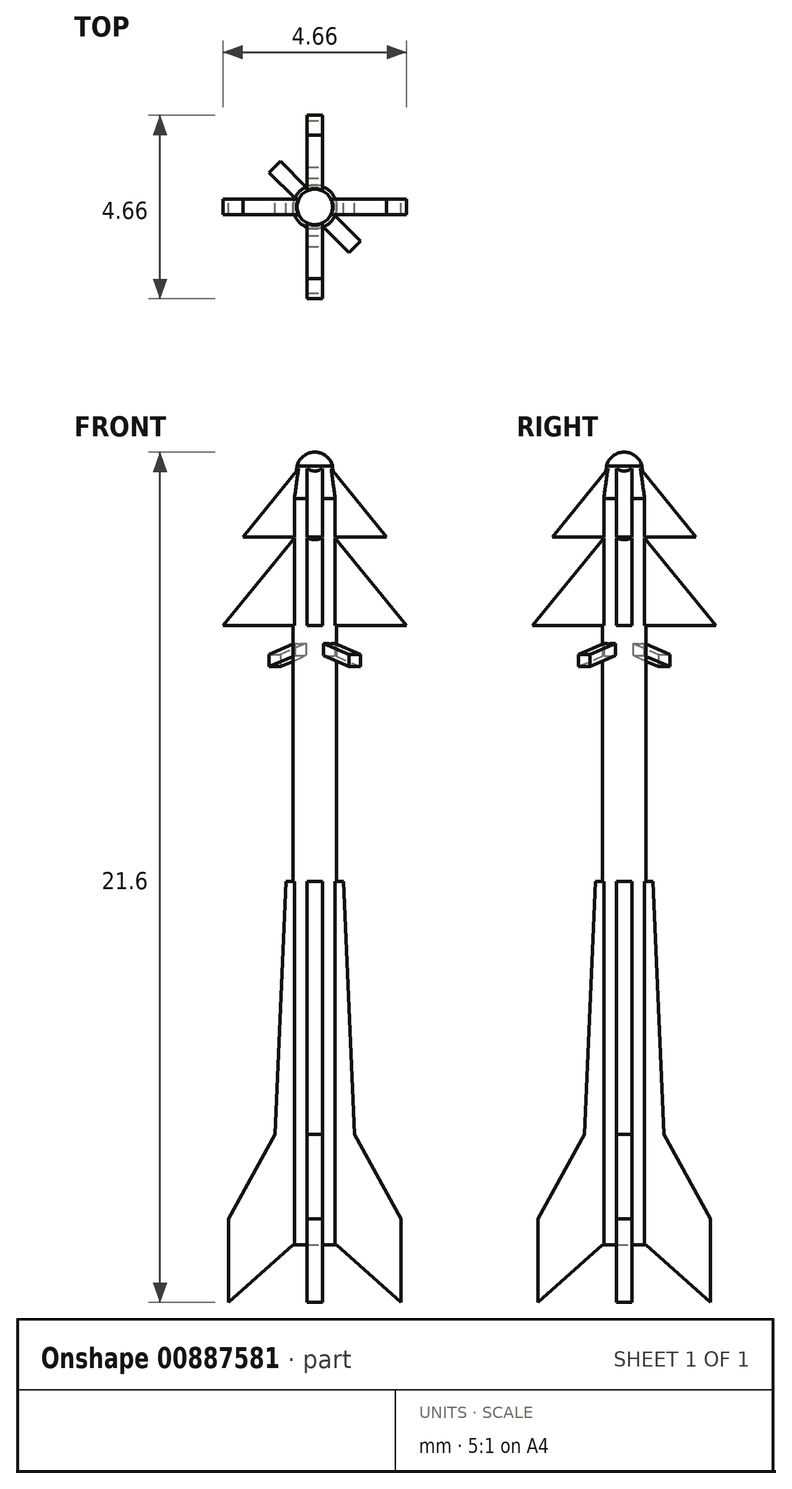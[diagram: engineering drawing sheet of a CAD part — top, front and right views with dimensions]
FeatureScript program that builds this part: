
annotation { "Feature Type Name" : "Feature", "Feature Type Description" : "" }
export const myFeature = defineFeature(function(context is Context, id is Id, definition is map)
    precondition{}
    {
        {
            var Q0;
            Q0=qCreatedBy(makeId("Front.planeOp"),FACE);
            var sketch = newSketch(context, id + "F0", { "sketchPlane" : qUnion([Q0])});
            skLineSegment(sketch, "E0", {"start": v(0, 0) * mm, "end": v(0, 20.14) * mm});
            skLineSegment(sketch, "E1", {"start": v(0.56, 18.96) * mm, "end": v(0.56, 0) * mm});
            skLineSegment(sketch, "E2", {"start": v(0.56, 0) * mm, "end": v(0, 0) * mm});
            skLineSegment(sketch, "E3", {"start": v(0, 20.14) * mm, "end": v(1.85, 20.14) * mm, "construction": true});
            skLineSegment(sketch, "E4", {"start": v(0.56, 18.96) * mm, "end": v(0.45, 19.8) * mm});
            skArc(sketch, "E5", {"start": v(0.45, 19.8) * mm, "mid": v(0.28, 20.04) * mm, "end": v(0, 20.14) * mm});
            skSolve(sketch);
        }
        {
            var Q0;
            Q0=qSketchRegion(id+"F0",true);
            var Q1;
            Q1=sQuery(id+"F0.wireOp",EDGE,"E0");
            revolve(context, id + "F1", {"surfaceOperationType" : NewSurfaceOperationType.NEW, "entities" : qUnion([Q0]), "axis" : qUnion([Q1]), "revolveType" : RevolveType.FULL});
        }
        {
            var Q0;
            Q0=qCreatedBy(makeId("Front.planeOp"),FACE);
            var sketch = newSketch(context, id + "F2", { "sketchPlane" : qUnion([Q0])});
            skLineSegment(sketch, "E6", {"start": v(-0.56, 0.19) * mm, "end": v(-0.56, 18.96) * mm, "construction": true});
            skLineSegment(sketch, "E7.0", {"start": v(0.56, 18.96) * mm, "end": v(-0.56, 18.96) * mm});
            skLineSegment(sketch, "E8", {"start": v(-0.23, 19.96) * mm, "end": v(-1.82, 17.99) * mm});
            skLineSegment(sketch, "E9", {"start": v(-1.82, 17.99) * mm, "end": v(-0.5, 17.99) * mm});
            skLineSegment(sketch, "E10", {"start": v(-0.5, 17.99) * mm, "end": v(-2.33, 15.73) * mm});
            skLineSegment(sketch, "E11", {"start": v(-2.33, 15.73) * mm, "end": v(2.33, 15.73) * mm});
            skLineSegment(sketch, "E12", {"start": v(2.33, 15.73) * mm, "end": v(0.5, 17.99) * mm});
            skLineSegment(sketch, "E13", {"start": v(0.5, 17.99) * mm, "end": v(1.82, 17.99) * mm});
            skLineSegment(sketch, "E14", {"start": v(1.82, 17.99) * mm, "end": v(0.23, 19.96) * mm});
            skLineSegment(sketch, "E15", {"start": v(0.23, 19.96) * mm, "end": v(-0.23, 19.96) * mm});
            skLineSegment(sketch, "E16.0", {"start": v(0.56, 0) * mm, "end": v(-0.56, 0) * mm});
            skLineSegment(sketch, "E17", {"start": v(-0.54, 0.02) * mm, "end": v(-2.19, -1.46) * mm});
            skLineSegment(sketch, "E18", {"start": v(-2.19, -1.46) * mm, "end": v(-2.19, 0.66) * mm});
            skLineSegment(sketch, "E19", {"start": v(-2.19, 0.66) * mm, "end": v(-1, 2.81) * mm});
            skLineSegment(sketch, "E20", {"start": v(-1, 2.81) * mm, "end": v(-0.73, 9.24) * mm});
            skLineSegment(sketch, "E21", {"start": v(-0.73, 9.24) * mm, "end": v(0.73, 9.24) * mm});
            skLineSegment(sketch, "E22", {"start": v(0.73, 9.24) * mm, "end": v(1, 2.81) * mm});
            skLineSegment(sketch, "E23", {"start": v(1, 2.81) * mm, "end": v(2.19, 0.66) * mm});
            skLineSegment(sketch, "E24", {"start": v(2.19, 0.66) * mm, "end": v(2.19, -1.46) * mm});
            skLineSegment(sketch, "E25", {"start": v(2.19, -1.46) * mm, "end": v(0.54, 0.02) * mm});
            skLineSegment(sketch, "E26", {"start": v(0.54, 0.02) * mm, "end": v(-0.54, 0.02) * mm});
            skLineSegment(sketch, "E27", {"start": v(0, 0) * mm, "end": v(0, 0.02) * mm, "construction": true});
            skLineSegment(sketch, "E28", {"start": v(0, 0) * mm, "end": v(0, 9.24) * mm, "construction": true});
            skPoint(sketch, "E28.endSnap0", {"position": v(0, 0) * mm});
            skLineSegment(sketch, "E29", {"start": v(0, 19.96) * mm, "end": v(0, 18.96) * mm, "construction": true});
            skLineSegment(sketch, "E30", {"start": v(0, 18.96) * mm, "end": v(0, 15.73) * mm, "construction": true});
            skPoint(sketch, "E31", {"position": v(-0.56, 17.92) * mm});
            skSolve(sketch);
        }
        {
            var Q0;
            Q0=qSketchRegion(id+"F2",true);
            extrude(context, id + "F3", {"entities" : qUnion([Q0]), "operationType" : NewBodyOperationType.ADD, "depth" : .4 * mm, "offsetDistance" : 25 * mm, "symmetric" : true});
        }
        {
            var Q0;
            Q0=makeQuery(id+"F1.opRevolve","SWEPT_BODY",BODY,{"disambiguationData":[OSD([sQuery(id+"F0.wireOp",EDGE,"E0"),sQuery(id+"F0.wireOp",EDGE,"E1"),sQuery(id+"F0.wireOp",EDGE,"E2"),sQuery(id+"F0.wireOp",EDGE,"m1K1lCZm-MTc8-Btmt-IA6e-LtdyprMEJuD3")])]});
            var Q1;
            Q1=makeQuery(id+"F1.opRevolve","SWEPT_FACE",FACE,{"disambiguationData":[OSD([sQuery(id+"F0.wireOp",EDGE,"E1")])]});
            circularPattern(context, id + "F4", {"entities" : qUnion([Q0]), "axis" : qUnion([Q1]), "angle" : 360 * degree, "instanceCount" : 4, "equalSpace" : true, "computeTransformsWithoutBuiltin" : true});
        }
        {
            var Q0;
            Q0=qCreatedBy(makeId("Front.planeOp"),FACE);
            var Q1;
            Q1=qCreatedBy(makeId("Right.planeOp"),FACE);
            cPlane(context, id + "F5", {"entities" : qUnion([Q0, Q1]), "cplaneType" : CPlaneType.MID_PLANE, "offset" : 25 * mm, "width" : 150 * mm, "height" : 150 * mm});
        }
        {
            var Q0;
            Q0=qCreatedBy(id+"F5.planeOp",FACE);
            var sketch = newSketch(context, id + "F6", { "sketchPlane" : qUnion([Q0])});
            skLineSegment(sketch, "E32", {"start": v(-0.25, 15.37) * mm, "end": v(-1.44, 15) * mm});
            skLineSegment(sketch, "E33", {"start": v(1.44, 15) * mm, "end": v(0.25, 15.37) * mm});
            skLineSegment(sketch, "E34", {"start": v(0.25, 15.37) * mm, "end": v(-0.25, 15.37) * mm});
            skPoint(sketch, "E35", {"position": v(-0.53, 15.28) * mm});
            skLineSegment(sketch, "E36", {"start": v(0, 0) * mm, "end": v(0, 15.05) * mm, "construction": true});
            skPoint(sketch, "E36.endSnap0", {"position": v(0, 15.05) * mm});
            skLineSegment(sketch, "E37", {"start": v(-1.44, 15) * mm, "end": v(-1.44, 14.69) * mm});
            skLineSegment(sketch, "E38", {"start": v(-1.44, 14.69) * mm, "end": v(-0.25, 15.05) * mm});
            skLineSegment(sketch, "E39", {"start": v(-0.25, 15.05) * mm, "end": v(0.25, 15.05) * mm});
            skLineSegment(sketch, "E40", {"start": v(0.25, 15.05) * mm, "end": v(1.44, 14.69) * mm});
            skLineSegment(sketch, "E41", {"start": v(1.44, 14.69) * mm, "end": v(1.44, 15) * mm});
            skPoint(sketch, "E42", {"position": v(0, 15.37) * mm});
            skLineSegment(sketch, "E43.0.0", {"start": v(-0.56, 0) * mm, "end": v(0.23, 0) * mm});
            skLineSegment(sketch, "E43.0.1", {"start": v(0.23, 0) * mm, "end": v(0.25, 0) * mm});
            skLineSegment(sketch, "E43.0.2", {"start": v(0.25, 0) * mm, "end": v(0.53, 0) * mm});
            skLineSegment(sketch, "E43.0.3", {"start": v(0.53, 0) * mm, "end": v(0.5, 0) * mm});
            skLineSegment(sketch, "E43.0.4", {"start": v(0.56, 0) * mm, "end": v(-0.23, 0) * mm});
            skLineSegment(sketch, "E43.0.5", {"start": v(-0.23, 0) * mm, "end": v(-0.25, 0) * mm});
            skLineSegment(sketch, "E43.0.6", {"start": v(-0.25, 0) * mm, "end": v(-0.53, 0) * mm});
            skLineSegment(sketch, "E43.0.7", {"start": v(-0.53, 0) * mm, "end": v(-0.5, 0) * mm});
            skSolve(sketch);
        }
        {
            var Q0;
            Q0=qSketchRegion(id+"F6",true);
            extrude(context, id + "F7", {"entities" : qUnion([Q0]), "operationType" : NewBodyOperationType.ADD, "depth" : .4 * mm, "offsetDistance" : 25 * mm, "symmetric" : true});
        }
    });
